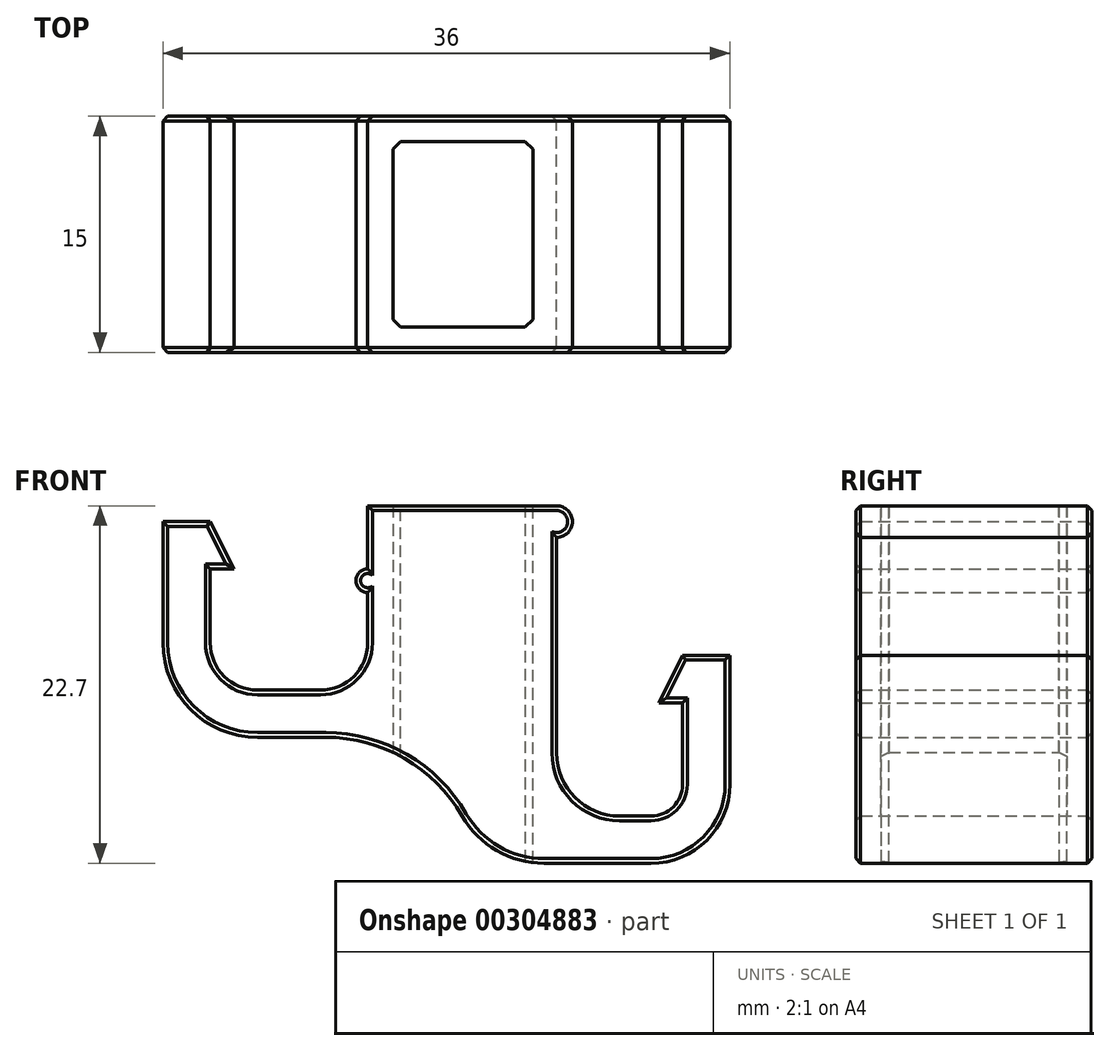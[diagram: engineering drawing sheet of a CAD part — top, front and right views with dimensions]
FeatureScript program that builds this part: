
annotation { "Feature Type Name" : "Feature", "Feature Type Description" : "" }
export const myFeature = defineFeature(function(context is Context, id is Id, definition is map)
    precondition{}
    {
        {
            var Q0;
            Q0=qCreatedBy(makeId("Front.planeOp"),FACE);
            var sketch = newSketch(context, id + "F0", { "sketchPlane" : qUnion([Q0])});
            skLineSegment(sketch, "E0", {"start": v(-6, 1) * mm, "end": v(-6, -3) * mm});
            skLineSegment(sketch, "E1", {"start": v(6, -1) * mm, "end": v(6, -14.7) * mm});
            skLineSegment(sketch, "E2", {"start": v(-16, -5.7) * mm, "end": v(-16, -3) * mm});
            skLineSegment(sketch, "E3", {"start": v(14, -14.7) * mm, "end": v(14, -11.5) * mm});
            skLineSegment(sketch, "E4", {"start": v(-16, -3) * mm, "end": v(-14.5, -3) * mm});
            skLineSegment(sketch, "E5", {"start": v(12.5, -11.5) * mm, "end": v(14, -11.5) * mm});
            skLineSegment(sketch, "E6", {"start": v(-16, -5.7) * mm, "end": v(-16, -7.7) * mm});
            skLineSegment(sketch, "E7", {"start": v(-13, -10.7) * mm, "end": v(-9, -10.7) * mm});
            skLineSegment(sketch, "E8", {"start": v(-6, -7.7) * mm, "end": v(-6, -5.7) * mm});
            skPoint(sketch, "E9.visualSharp", {"position": v(-16, -10.7) * mm});
            skArc(sketch, "E9.filletArc", {"start": v(-16, -7.7) * mm, "mid": v(-15.12, -9.82) * mm, "end": v(-13, -10.7) * mm});
            skPoint(sketch, "E10.visualSharp", {"position": v(-6, -10.7) * mm});
            skArc(sketch, "E10.filletArc", {"start": v(-9, -10.7) * mm, "mid": v(-6.88, -9.82) * mm, "end": v(-6, -7.7) * mm});
            skLineSegment(sketch, "E11", {"start": v(-14.5, -3) * mm, "end": v(-16, 0) * mm});
            skLineSegment(sketch, "E12", {"start": v(-16, 0) * mm, "end": v(-19, 0) * mm});
            skLineSegment(sketch, "E13", {"start": v(-19, 0) * mm, "end": v(-19, -7.7) * mm});
            skLineSegment(sketch, "E14", {"start": v(-13, -13.7) * mm, "end": v(-8.66, -13.7) * mm});
            skLineSegment(sketch, "E15", {"start": v(5.2, -21.7) * mm, "end": v(12, -21.7) * mm});
            skLineSegment(sketch, "E16", {"start": v(17, -16.7) * mm, "end": v(17, -8.5) * mm});
            skLineSegment(sketch, "E17", {"start": v(17, -8.5) * mm, "end": v(14, -8.5) * mm});
            skLineSegment(sketch, "E18", {"start": v(14, -8.5) * mm, "end": v(12.5, -11.5) * mm});
            skPoint(sketch, "E19.visualSharp", {"position": v(-19, -13.7) * mm});
            skArc(sketch, "E19.filletArc", {"start": v(-19, -7.7) * mm, "mid": v(-17.24, -11.94) * mm, "end": v(-13, -13.7) * mm});
            skPoint(sketch, "E20.visualSharp", {"position": v(17, -21.7) * mm});
            skArc(sketch, "E20.filletArc", {"start": v(12, -21.7) * mm, "mid": v(15.54, -20.24) * mm, "end": v(17, -16.7) * mm});
            skPoint(sketch, "E21.visualSharp", {"position": v(-3.35, -21.7) * mm});
            skArc(sketch, "E21.filletArc", {"start": v(0, -18.7) * mm, "mid": v(2.2, -20.9) * mm, "end": v(5.2, -21.7) * mm});
            skPoint(sketch, "E22.visualSharp", {"position": v(0, -13.7) * mm});
            skArc(sketch, "E22.filletArc", {"start": v(0, -18.7) * mm, "mid": v(-3.66, -15.04) * mm, "end": v(-8.66, -13.7) * mm});
            skLineSegment(sketch, "E23", {"start": v(0, -18.7) * mm, "end": v(0, -3.06) * mm});
            skLineSegment(sketch, "E24", {"start": v(-6, 1) * mm, "end": v(6, 1) * mm});
            skPoint(sketch, "E25.center.orphan", {"position": v(10, -13.3) * mm});
            skLineSegment(sketch, "E26", {"start": v(6, -14.7) * mm, "end": v(6, -14.7) * mm});
            skLineSegment(sketch, "E27", {"start": v(10, -18.7) * mm, "end": v(12, -18.7) * mm});
            skLineSegment(sketch, "E28", {"start": v(14, -16.7) * mm, "end": v(14, -14.7) * mm});
            skPoint(sketch, "E29.visualSharp", {"position": v(14, -18.7) * mm});
            skArc(sketch, "E29.filletArc", {"start": v(12, -18.7) * mm, "mid": v(13.41, -18.11) * mm, "end": v(14, -16.7) * mm});
            skPoint(sketch, "E30.visualSharp", {"position": v(6, -18.7) * mm});
            skArc(sketch, "E30.filletArc", {"start": v(6, -14.7) * mm, "mid": v(7.17, -17.53) * mm, "end": v(10, -18.7) * mm});
            skPoint(sketch, "E31.orphan", {"position": v(10, -11.5) * mm});
            skPoint(sketch, "E32.orphan", {"position": v(-6, 13.07) * mm});
            skPoint(sketch, "E33.orphan", {"position": v(10, 13.27) * mm});
            skPoint(sketch, "E34.start.orphan", {"position": v(-16.23, 13.07) * mm});
            skArc(sketch, "E35", {"start": v(-6, -3) * mm, "mid": v(-6.75, -3.75) * mm, "end": v(-6, -4.5) * mm});
            skArc(sketch, "E36", {"start": v(6, -1) * mm, "mid": v(7, 0) * mm, "end": v(6, 1) * mm});
            skLineSegment(sketch, "E37.trimOffspring", {"start": v(-6, -4.5) * mm, "end": v(-6, -5.7) * mm});
            skSolve(sketch);
        }
        {
            var Q0;
            Q0=makeQuery(id+"F0.imprint","IMPRINT",FACE,{"disambiguationData":[TD([[makeQuery(id+"F0.imprint","IMPRINT",EDGE,{"derivedFrom":sQuery(id+"F0.wireOp",EDGE,"E2")}),1.0]])]});
            extrude(context, id + "F1", {"entities" : qUnion([Q0]), "depth" : 15 * mm});
        }
        {
            var Q0;
            Q0=makeQuery(id+"F1.opExtrude","SWEPT_FACE",FACE,{"disambiguationData":[OSD([sQuery(id+"F0.wireOp",EDGE,"E24")])]});
            var sketch = newSketch(context, id + "F2", { "sketchPlane" : qUnion([Q0])});
            skLineSegment(sketch, "E38.0", {"start": v(-4.4, -15) * mm, "end": v(-4.4, 0) * mm});
            skLineSegment(sketch, "E39.0", {"start": v(4.5, -1.6) * mm, "end": v(-4.4, -1.6) * mm});
            skLineSegment(sketch, "E39.1", {"start": v(4.5, -13.4) * mm, "end": v(4.5, -1.6) * mm});
            skLineSegment(sketch, "E39.2", {"start": v(-4.4, -13.4) * mm, "end": v(4.5, -13.4) * mm});
            skLineSegment(sketch, "E39.3", {"start": v(-4.4, -1.6) * mm, "end": v(-4.4, -13.4) * mm});
            skSolve(sketch);
        }
        {
            var Q0;
            Q0=makeQuery(id+"F2.imprint","IMPRINT",FACE,{"disambiguationData":[TD([[makeQuery(id+"F2.imprint","IMPRINT",EDGE,{"derivedFrom":sQuery(id+"F2.wireOp",EDGE,"E39.0")}),1.0]])]});
            extrude(context, id + "F3", {"entities" : qUnion([Q0]), "operationType" : NewBodyOperationType.REMOVE, "oppositeDirection" : true, "depth" : 25 * mm});
        }
        {
            var Q0;
            Q0=makeQuery(id+"F1.opExtrude","CAP_FACE",FACE,{"disambiguationData":[OSD([sQuery(id+"F0.wireOp",EDGE,"E0"),sQuery(id+"F0.wireOp",EDGE,"E1"),sQuery(id+"F0.wireOp",EDGE,"E25"),sQuery(id+"F0.wireOp",EDGE,"E2"),sQuery(id+"F0.wireOp",EDGE,"E3"),sQuery(id+"F0.wireOp",EDGE,"E4"),sQuery(id+"F0.wireOp",EDGE,"E5"),sQuery(id+"F0.wireOp",EDGE,"E6"),sQuery(id+"F0.wireOp",EDGE,"E7"),sQuery(id+"F0.wireOp",EDGE,"E8"),sQuery(id+"F0.wireOp",EDGE,"E9.filletArc"),sQuery(id+"F0.wireOp",EDGE,"E10.filletArc"),sQuery(id+"F0.wireOp",EDGE,"E11"),sQuery(id+"F0.wireOp",EDGE,"E12"),sQuery(id+"F0.wireOp",EDGE,"E13"),sQuery(id+"F0.wireOp",EDGE,"E14"),sQuery(id+"F0.wireOp",EDGE,"E15"),sQuery(id+"F0.wireOp",EDGE,"E16"),sQuery(id+"F0.wireOp",EDGE,"E17"),sQuery(id+"F0.wireOp",EDGE,"E18"),sQuery(id+"F0.wireOp",EDGE,"E19.filletArc"),sQuery(id+"F0.wireOp",EDGE,"E20.filletArc"),sQuery(id+"F0.wireOp",EDGE,"E21.filletArc"),sQuery(id+"F0.wireOp",EDGE,"E22.filletArc"),sQuery(id+"F0.wireOp",EDGE,"E24")])],"isStart":false});
            var Q1;
            Q1=makeQuery(id+"F1.opExtrude","CAP_FACE",FACE,{"disambiguationData":[OSD([sQuery(id+"F0.wireOp",EDGE,"E0"),sQuery(id+"F0.wireOp",EDGE,"E1"),sQuery(id+"F0.wireOp",EDGE,"E25"),sQuery(id+"F0.wireOp",EDGE,"E2"),sQuery(id+"F0.wireOp",EDGE,"E3"),sQuery(id+"F0.wireOp",EDGE,"E4"),sQuery(id+"F0.wireOp",EDGE,"E5"),sQuery(id+"F0.wireOp",EDGE,"E6"),sQuery(id+"F0.wireOp",EDGE,"E7"),sQuery(id+"F0.wireOp",EDGE,"E8"),sQuery(id+"F0.wireOp",EDGE,"E9.filletArc"),sQuery(id+"F0.wireOp",EDGE,"E10.filletArc"),sQuery(id+"F0.wireOp",EDGE,"E11"),sQuery(id+"F0.wireOp",EDGE,"E12"),sQuery(id+"F0.wireOp",EDGE,"E13"),sQuery(id+"F0.wireOp",EDGE,"E14"),sQuery(id+"F0.wireOp",EDGE,"E15"),sQuery(id+"F0.wireOp",EDGE,"E16"),sQuery(id+"F0.wireOp",EDGE,"E17"),sQuery(id+"F0.wireOp",EDGE,"E18"),sQuery(id+"F0.wireOp",EDGE,"E19.filletArc"),sQuery(id+"F0.wireOp",EDGE,"E20.filletArc"),sQuery(id+"F0.wireOp",EDGE,"E21.filletArc"),sQuery(id+"F0.wireOp",EDGE,"E22.filletArc"),sQuery(id+"F0.wireOp",EDGE,"E24")])],"isStart":true});
            chamfer(context, id + "F4", {"entities" : qUnion([Q0, Q1]), "width" : 0.3 * mm, "tangentPropagation" : true});
        }
        {
            var Q0;
            Q0=makeQuery(id+"F3.boolean.opBoolean","COPY",EDGE,{"derivedFrom":makeQuery(id+"F3.opExtrude","SWEPT_EDGE",EDGE,{"disambiguationData":[OSD([sQuery(id+"F2.wireOp",EDGE,"E38.0"),sQuery(id+"F2.wireOp",EDGE,"E39.2"),sQuery(id+"F2.wireOp",EDGE,"E39.3")])]})});
            var Q1;
            Q1=makeQuery(id+"F3.boolean.opBoolean","COPY",EDGE,{"derivedFrom":makeQuery(id+"F3.opExtrude","SWEPT_EDGE",EDGE,{"disambiguationData":[OSD([sQuery(id+"F2.wireOp",EDGE,"E39.1"),sQuery(id+"F2.wireOp",EDGE,"E39.2")])]})});
            var Q2;
            Q2=makeQuery(id+"F3.boolean.opBoolean","COPY",EDGE,{"derivedFrom":makeQuery(id+"F3.opExtrude","SWEPT_EDGE",EDGE,{"disambiguationData":[OSD([sQuery(id+"F2.wireOp",EDGE,"E39.0"),sQuery(id+"F2.wireOp",EDGE,"E39.1")])]})});
            var Q3;
            Q3=makeQuery(id+"F3.boolean.opBoolean","COPY",EDGE,{"derivedFrom":makeQuery(id+"F3.opExtrude","SWEPT_EDGE",EDGE,{"disambiguationData":[OSD([sQuery(id+"F2.wireOp",EDGE,"E38.0"),sQuery(id+"F2.wireOp",EDGE,"E39.0"),sQuery(id+"F2.wireOp",EDGE,"E39.3")])]})});
            chamfer(context, id + "F5", {"entities" : qUnion([Q0, Q1, Q2, Q3]), "width" : .5 * mm, "tangentPropagation" : true});
        }
    });
